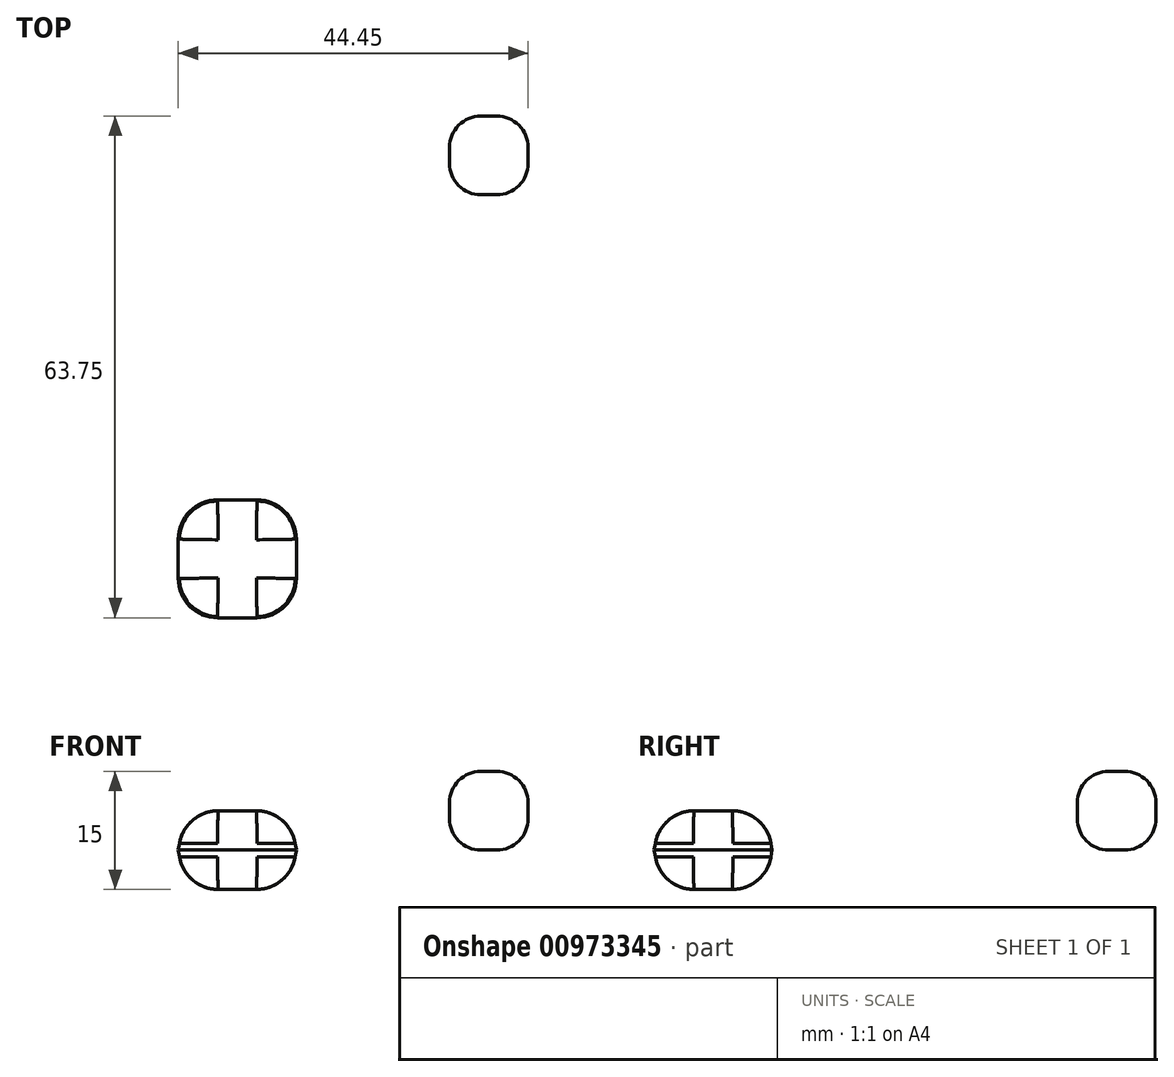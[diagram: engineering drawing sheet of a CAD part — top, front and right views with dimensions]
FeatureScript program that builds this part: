
annotation { "Feature Type Name" : "Feature", "Feature Type Description" : "" }
export const myFeature = defineFeature(function(context is Context, id is Id, definition is map)
    precondition{}
    {
        {
            var Q0;
            Q0=qCreatedBy(makeId("Top.planeOp"),FACE);
            var sketch = newSketch(context, id + "F0", { "sketchPlane" : qUnion([Q0])});
            skLineSegment(sketch, "E0.bottom", {"start": v(5, 5) * mm, "end": v(-5, 5) * mm});
            skLineSegment(sketch, "E0.top", {"start": v(5, -5) * mm, "end": v(-5, -5) * mm});
            skLineSegment(sketch, "E0.left", {"start": v(5, 5) * mm, "end": v(5, -5) * mm});
            skLineSegment(sketch, "E0.right", {"start": v(-5, 5) * mm, "end": v(-5, -5) * mm});
            skPoint(sketch, "E0.middle", {"position": v(0, 0) * mm});
            skSolve(sketch);
        }
        {
            var Q0;
            Q0 = qSketchRegion(id + "F0", true);
            extrude(context, id + "F1", {"entities" : qUnion([Q0]), "depth" : 10 * mm, "offsetDistance" : 25 * mm});
        }
        {
            var Q0;
            Q0=makeQuery(id+"F1.opExtrude","SWEPT_FACE",FACE,{"disambiguationData":[OSD([sQuery(id+"F0.wireOp",EDGE,"E0.top")])]});
            var Q1;
            Q1=makeQuery(id+"F1.opExtrude","SWEPT_FACE",FACE,{"disambiguationData":[OSD([sQuery(id+"F0.wireOp",EDGE,"E0.right")])]});
            var Q2;
            Q2=makeQuery(id+"F1.opExtrude","SWEPT_FACE",FACE,{"disambiguationData":[OSD([sQuery(id+"F0.wireOp",EDGE,"E0.bottom")])]});
            var Q3;
            Q3=makeQuery(id+"F1.opExtrude","SWEPT_FACE",FACE,{"disambiguationData":[OSD([sQuery(id+"F0.wireOp",EDGE,"E0.left")])]});
            fillet(context, id + "F2", {"entities" : qUnion([Q0, Q1, Q2, Q3]), "radius" : 4 * mm, "tangentPropagation" : true, "allowEdgeOverflow" : false});
        }
        {
            var Q0;
            Q0=qCreatedBy(makeId("Top.planeOp"),FACE);
            var sketch = newSketch(context, id + "F3", { "sketchPlane" : qUnion([Q0])});
            skLineSegment(sketch, "E1.bottom", {"start": v(-34.45, -43.75) * mm, "end": v(-29.45, -43.75) * mm});
            skLineSegment(sketch, "E1.top", {"start": v(-34.45, -58.75) * mm, "end": v(-29.45, -58.75) * mm});
            skLineSegment(sketch, "E1.left", {"start": v(-39.45, -48.75) * mm, "end": v(-39.45, -53.75) * mm});
            skLineSegment(sketch, "E1.right", {"start": v(-24.45, -48.75) * mm, "end": v(-24.45, -53.75) * mm});
            skPoint(sketch, "E1.middle", {"position": v(-31.95, -51.25) * mm});
            skPoint(sketch, "E2.visualSharp", {"position": v(-39.45, -58.75) * mm});
            skArc(sketch, "E2.filletArc", {"start": v(-39.45, -53.75) * mm, "mid": v(-37.98, -57.29) * mm, "end": v(-34.45, -58.75) * mm});
            skPoint(sketch, "E3.visualSharp", {"position": v(-39.45, -43.75) * mm});
            skArc(sketch, "E3.filletArc", {"start": v(-34.45, -43.75) * mm, "mid": v(-37.98, -45.22) * mm, "end": v(-39.45, -48.75) * mm});
            skPoint(sketch, "E4.visualSharp", {"position": v(-24.45, -43.75) * mm});
            skArc(sketch, "E4.filletArc", {"start": v(-24.45, -48.75) * mm, "mid": v(-25.91, -45.22) * mm, "end": v(-29.45, -43.75) * mm});
            skPoint(sketch, "E5.visualSharp", {"position": v(-24.45, -58.75) * mm});
            skArc(sketch, "E5.filletArc", {"start": v(-29.45, -58.75) * mm, "mid": v(-25.91, -57.29) * mm, "end": v(-24.45, -53.75) * mm});
            skSolve(sketch);
        }
        {
            var Q0;
            Q0 = qSketchRegion(id + "F3", true);
            extrude(context, id + "F4", {"entities" : qUnion([Q0]), "depth" : 10 * mm, "offsetDistance" : 25 * mm, "hasDraft" : true, "draftAngle" : 10 * degree, "draftPullDirection" : true, "symmetric" : true});
        }
        {
            var Q0;
            Q0=makeQuery(id+"F4.opExtrude","CAP_FACE",FACE,{"disambiguationData":[OSD([sQuery(id+"F3.wireOp",EDGE,"E1.bottom"),sQuery(id+"F3.wireOp",EDGE,"E1.top"),sQuery(id+"F3.wireOp",EDGE,"E1.left"),sQuery(id+"F3.wireOp",EDGE,"E1.right"),sQuery(id+"F3.wireOp",EDGE,"E2.filletArc"),sQuery(id+"F3.wireOp",EDGE,"E3.filletArc"),sQuery(id+"F3.wireOp",EDGE,"E4.filletArc"),sQuery(id+"F3.wireOp",EDGE,"E5.filletArc")])],"isStart":true});
            var Q1;
            Q1=makeQuery(id+"F4.opExtrude","CAP_FACE",FACE,{"disambiguationData":[OSD([sQuery(id+"F3.wireOp",EDGE,"E1.bottom"),sQuery(id+"F3.wireOp",EDGE,"E1.top"),sQuery(id+"F3.wireOp",EDGE,"E1.left"),sQuery(id+"F3.wireOp",EDGE,"E1.right"),sQuery(id+"F3.wireOp",EDGE,"E2.filletArc"),sQuery(id+"F3.wireOp",EDGE,"E3.filletArc"),sQuery(id+"F3.wireOp",EDGE,"E4.filletArc"),sQuery(id+"F3.wireOp",EDGE,"E5.filletArc")])],"isStart":false});
            fillet(context, id + "F5", {"entities" : qUnion([Q0, Q1]), "tangentPropagation" : true, "radius" : 5 * mm, "defaultsChanged" : false, "vertexSettings" : [], "allowEdgeOverflow" : false});
        }
    });
